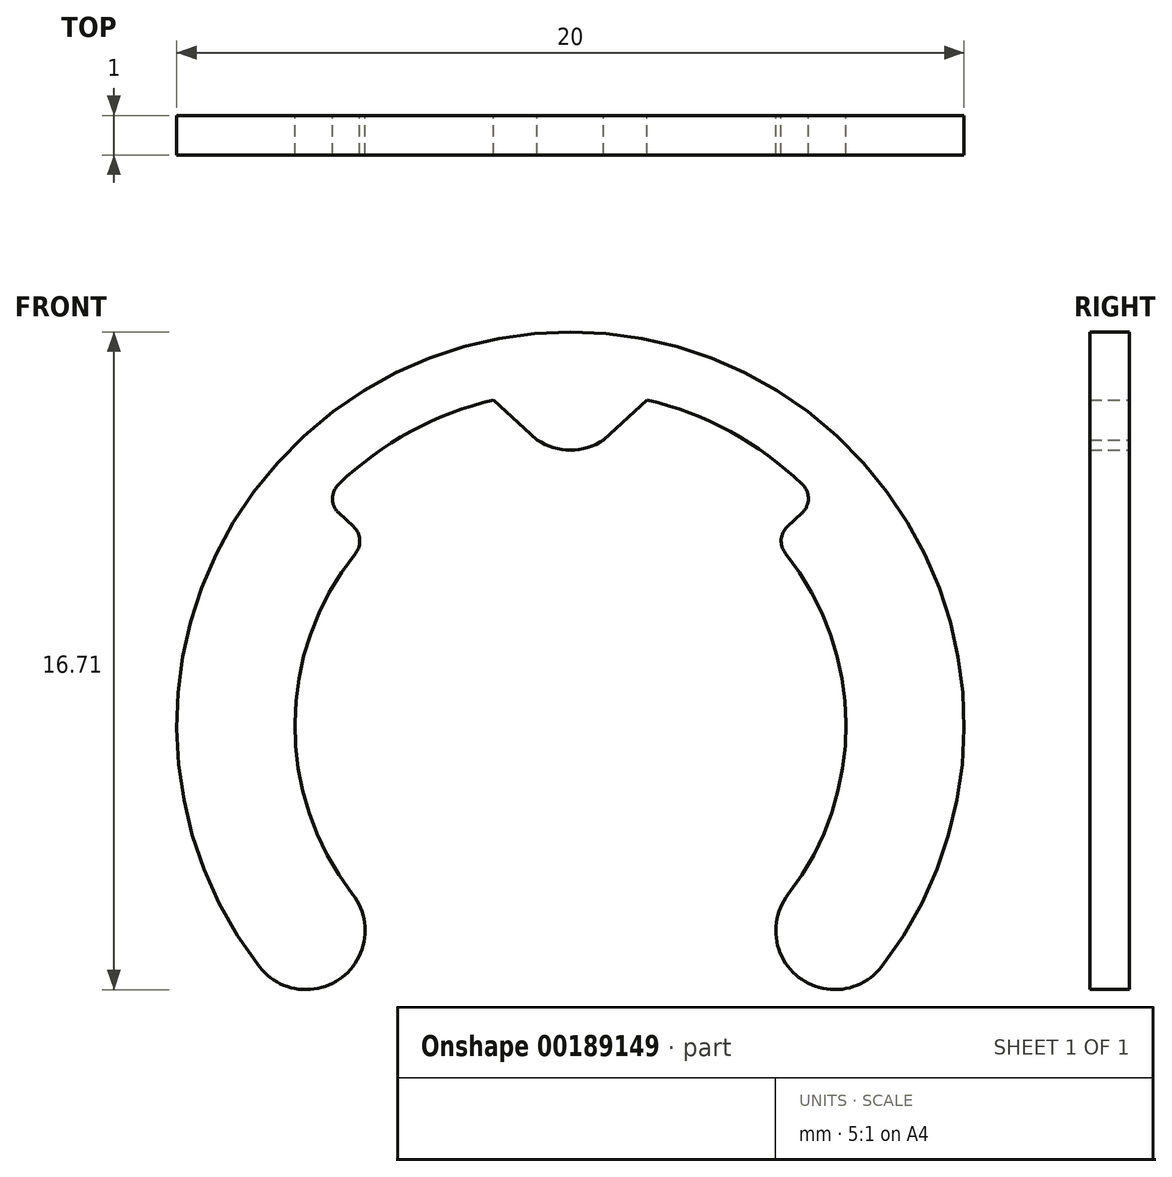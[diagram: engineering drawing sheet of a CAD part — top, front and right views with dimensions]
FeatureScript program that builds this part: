
annotation { "Feature Type Name" : "Feature", "Feature Type Description" : "" }
export const myFeature = defineFeature(function(context is Context, id is Id, definition is map)
    precondition{}
    {
        {
            var Q0;
            Q0=qCreatedBy(makeId("Front.planeOp"),FACE);
            var sketch = newSketch(context, id + "F0", { "sketchPlane" : qUnion([Q0])});
            skArc(sketch, "E0", {"start": v(7.9, -6.13) * mm, "mid": v(0, 10) * mm, "end": v(-7.9, -6.13) * mm});
            skArc(sketch, "E1.0", {"start": v(5.53, -4.29) * mm, "mid": v(7, 0.06) * mm, "end": v(5.46, 4.38) * mm});
            skArc(sketch, "E2.0", {"start": v(5.9, 6.13) * mm, "mid": v(4.06, 7.47) * mm, "end": v(1.95, 8.27) * mm});
            skArc(sketch, "E3", {"start": v(-1.16, 7.55) * mm, "mid": v(0, 7) * mm, "end": v(1.16, 7.55) * mm});
            skLineSegment(sketch, "E4", {"start": v(-0.84, 7.26) * mm, "end": v(-1.95, 8.27) * mm});
            skLineSegment(sketch, "E5", {"start": v(-5.88, 5.4) * mm, "end": v(-5.51, 5.06) * mm});
            skLineSegment(sketch, "E6", {"start": v(0.84, 7.26) * mm, "end": v(1.95, 8.27) * mm});
            skLineSegment(sketch, "E7", {"start": v(5.88, 5.4) * mm, "end": v(5.51, 5.06) * mm});
            skLineSegment(sketch, "E8", {"start": v(5.7, -6.31) * mm, "end": v(5.6, -6.21) * mm});
            skLineSegment(sketch, "E9", {"start": v(-5.7, -6.31) * mm, "end": v(-5.6, -6.21) * mm});
            skArc(sketch, "E10.trimOffspring", {"start": v(-5.46, 4.38) * mm, "mid": v(-7, 0.06) * mm, "end": v(-5.53, -4.29) * mm});
            skArc(sketch, "E11", {"start": v(-7.9, -6.13) * mm, "mid": v(-5.8, -6.4) * mm, "end": v(-5.53, -4.29) * mm});
            skArc(sketch, "E12", {"start": v(5.53, -4.29) * mm, "mid": v(5.8, -6.4) * mm, "end": v(7.9, -6.13) * mm});
            skPoint(sketch, "E13.orphan", {"position": v(-4.69, -5.2) * mm});
            skPoint(sketch, "E14.orphan", {"position": v(-6.7, -7.43) * mm});
            skPoint(sketch, "E15.orphan", {"position": v(4.69, -5.2) * mm});
            skPoint(sketch, "E16.orphan", {"position": v(6.7, -7.43) * mm});
            skPoint(sketch, "E17.newPointB", {"position": v(6.26, 5.75) * mm});
            skArc(sketch, "E17.filletArc", {"start": v(5.88, 5.4) * mm, "mid": v(6.05, 5.76) * mm, "end": v(5.9, 6.13) * mm});
            skArc(sketch, "E18.trimOffspring", {"start": v(-6.72, -5.2) * mm, "mid": v(-6.23, -5.78) * mm, "end": v(-5.7, -6.31) * mm});
            skPoint(sketch, "E19.visualSharp", {"position": v(-6.26, 5.75) * mm});
            skArc(sketch, "E19.filletArc", {"start": v(-5.9, 6.13) * mm, "mid": v(-6.05, 5.76) * mm, "end": v(-5.88, 5.4) * mm});
            skPoint(sketch, "E20.visualSharp", {"position": v(-5.16, 4.73) * mm});
            skArc(sketch, "E20.filletArc", {"start": v(-5.46, 4.38) * mm, "mid": v(-5.35, 4.73) * mm, "end": v(-5.51, 5.06) * mm});
            skPoint(sketch, "E21.visualSharp", {"position": v(5.16, 4.73) * mm});
            skArc(sketch, "E21.filletArc", {"start": v(5.51, 5.06) * mm, "mid": v(5.35, 4.73) * mm, "end": v(5.46, 4.38) * mm});
            skArc(sketch, "E22.trimOffspring", {"start": v(-1.95, 8.27) * mm, "mid": v(-4.06, 7.47) * mm, "end": v(-5.9, 6.13) * mm});
            skSolve(sketch);
        }
        {
            var Q0;
            {var subQ1=sQuery(id+"F0.wireOp",EDGE,"E0");Q0=makeQuery(id+"F0.imprint","IMPRINT",FACE,{"disambiguationData":[TD([[makeQuery(id+"F0.imprint","IMPRINT",EDGE,{"derivedFrom":subQ1}),1.0]])]});}
            extrude(context, id + "F1", {"entities" : qUnion([Q0]), "depth" : 1 * mm});
        }
    });
